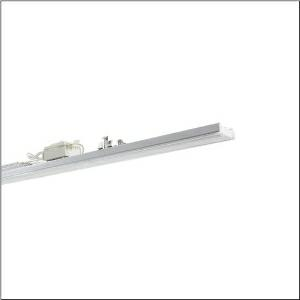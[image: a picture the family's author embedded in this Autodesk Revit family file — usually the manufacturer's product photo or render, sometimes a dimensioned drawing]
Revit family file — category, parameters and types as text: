
# Revit family: licross_r__21_recessed_ho_52te12dv4l2m3s4_36cd
name_source: partatom
category: Lighting Fixtures
units: mm (PartAtom-declared; Revit-internal decimal feet)

## family parameters
Cut with Voids When Loaded = No
Host = Face
Light Source = No
Part Type = Normal
Room Calculation Point = No
Round Connector Dimension = Use Diameter
Shared = No

## types (1)
- --- (1 x LED, 910 lm, 6.4 W, 4000K)
    Apparent Load = 6 VA
    CIE Flux Codes = 69 91 98 100 100
    Color Rendering = 80
    Color Temperature = 4000K
    Default Elevation = 1800 mm
    Description = Licross® 21 Recessed HO, luminaire insert, of sheet steel, galvanised, coil coated, white, length: 2.250mm, width: 66mm, height: 67mm, LED rated luminous flux: 22.710lm, light colour: 840, control gear: DALI 2, with plug, 6-pole, with phase selection, for trunking rail, 9 or 11-core, mains connection: 220..240V, AC, 50/60Hz, rated input power: 129W, for trunking rail, 9-/11-core, internal wiring halogen-free, for emergency light function, converter,control gear: single battery element, battery: LiFePO4, 9Ah, primary optical cover: cover, of PMMA, light emission: direct distribution, primary light characteristic: symmetric, protection rating (complete): IP54, insulation class (complete): insulation class I (protective earthing), certification: CE, UKCA, protection symbol: D if used in an environment with non-conductive dust loads with corresponding accessories, impact resistance: IK06, permissible ambient temperature for indoor applications: +5..+30°C, standard: EN 60598-2-22, LABS conformity tested according to VDMA 24364:2018-05, reducing of maximum allowable ambient temperature of 5°C with ceiling mounting, corresponds to IFS (International Featured Standards) requirements for safety and quality in the food industry, packaging unit: 1 piece
    Height = 58 mm
    Lamp = 1 x LED
    Lamp Light Flux = 910 lm
    Lamp Power = 6.4 W
    Lamp count = 1
    Length = 2250 mm
    Luminous efficacy = 142 lm/W
    Manufacturer = Siteco
    ModVariant = No
    Model = 52TE12DV4L2M3S4
    Mounting Place = Ceiling
    Mounting Type = Pendant
    Number of Poles = 1
    OnlyDefault = Yes
    Power Factor = 1
    Product Name = Licross® 21 Recessed HO
    Product group = luminaire insert | ceiling pendant
    ProductGroupID = 902
    Protection Class = Protection class I
    Protection Degree = IP 54
    RLX_Detail_Level = 1
    RLX_Emergency_Light_Flux = 0 lm
    RLX_Emergency_Type = 0
    RLX_Emergency_Type_DB = No
    RlxData = <blob elided: 30113 chars, md5=8838516e>
    Socket = socket
    Standby Power = 0 W
    System Light Flux = 910 lm
    System Power = 6 W
    Type Comments = : emergency light operation: 3 h
    Type Image = l_1296930.jpg
    URL = http://relux.com
    VarID = @adj_130759
    Voltage = 0 V
    Weight = 0.00 kg
    Width = 66 mm

## geometry (parser evidence)
native form markers: Blend x4, Sweep x8
no freeform markers — native parametric forms only
